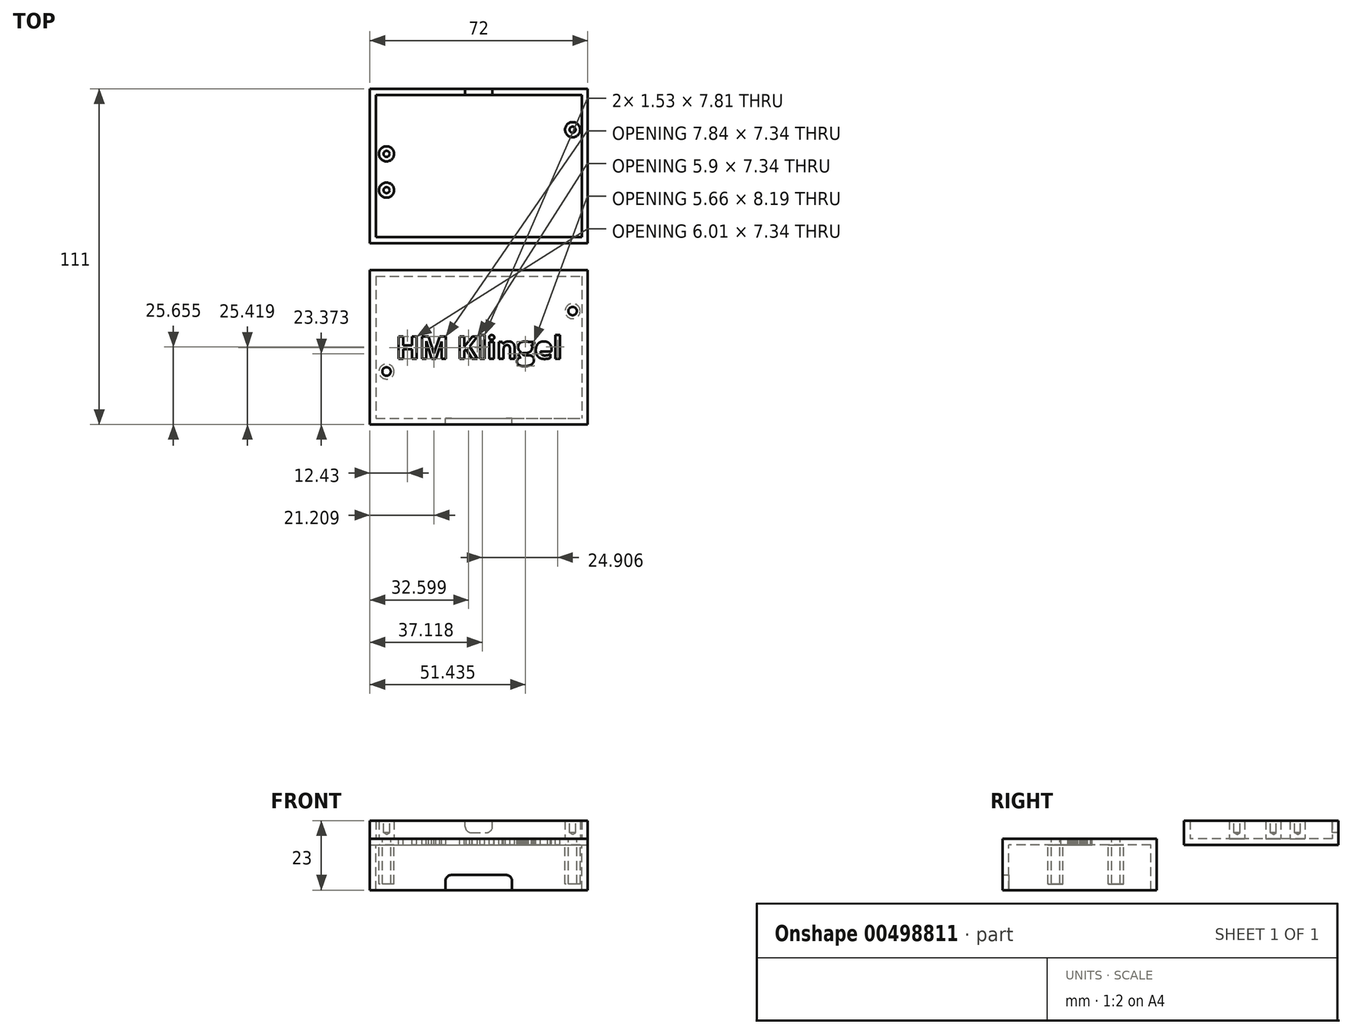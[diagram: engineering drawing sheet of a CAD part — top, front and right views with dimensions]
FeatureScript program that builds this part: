
annotation { "Feature Type Name" : "Feature", "Feature Type Description" : "" }
export const myFeature = defineFeature(function(context is Context, id is Id, definition is map)
    precondition{}
    {
        {
            var Q0;
            Q0=qCreatedBy(makeId("Top.planeOp"),FACE);
            var sketch = newSketch(context, id + "F0", { "sketchPlane" : qUnion([Q0])});
            skLineSegment(sketch, "E0.bottom", {"start": v(-45.23, 18.38) * mm, "end": v(22.77, 18.38) * mm});
            skLineSegment(sketch, "E0.top", {"start": v(-45.23, -28.62) * mm, "end": v(22.77, -28.62) * mm});
            skLineSegment(sketch, "E0.left", {"start": v(-45.23, 18.38) * mm, "end": v(-45.23, -28.62) * mm});
            skLineSegment(sketch, "E0.right", {"start": v(22.77, 18.38) * mm, "end": v(22.77, -28.62) * mm});
            skLineSegment(sketch, "E1.bottom", {"start": v(-47.23, 20.38) * mm, "end": v(24.77, 20.38) * mm});
            skLineSegment(sketch, "E1.top", {"start": v(-47.23, -30.62) * mm, "end": v(24.77, -30.62) * mm});
            skLineSegment(sketch, "E1.left", {"start": v(-47.23, 20.38) * mm, "end": v(-47.23, -30.62) * mm});
            skLineSegment(sketch, "E1.right", {"start": v(24.77, 20.38) * mm, "end": v(24.77, -30.62) * mm});
            skLineSegment(sketch, "E2", {"start": v(-11.23, 20.38) * mm, "end": v(-11.23, 18.38) * mm, "construction": true});
            skLineSegment(sketch, "E3", {"start": v(24.77, -5.12) * mm, "end": v(22.77, -5.12) * mm, "construction": true});
            skLineSegment(sketch, "E4", {"start": v(-45.23, -5.12) * mm, "end": v(-47.23, -5.12) * mm, "construction": true});
            skLineSegment(sketch, "E5", {"start": v(-11.23, -30.62) * mm, "end": v(-11.23, -28.62) * mm, "construction": true});
            skLineSegment(sketch, "E6", {"start": v(19.77, -28.62) * mm, "end": v(19.77, 6.88) * mm, "construction": true});
            skLineSegment(sketch, "E7", {"start": v(19.77, 6.88) * mm, "end": v(22.77, 6.88) * mm, "construction": true});
            skCircle(sketch, "E8", {"center": v(19.77, 6.88) * mm, "radius": 2.5 * mm});
            skLineSegment(sketch, "E9", {"start": v(-41.73, -28.62) * mm, "end": v(-41.73, -1.12) * mm, "construction": true});
            skLineSegment(sketch, "E10", {"start": v(-41.73, -1.12) * mm, "end": v(-45.23, -1.12) * mm, "construction": true});
            skCircle(sketch, "E11", {"center": v(-41.73, -1.12) * mm, "radius": 2.5 * mm});
            skPoint(sketch, "E12", {"position": v(-41.73, -13.12) * mm});
            skCircle(sketch, "E13", {"center": v(-41.73, -13.12) * mm, "radius": 2.5 * mm});
            skSolve(sketch);
        }
        {
            var Q0;
            Q0=makeQuery(id+"F0.imprint","IMPRINT",FACE,{"disambiguationData":[TD([[makeQuery(id+"F0.imprint","IMPRINT",EDGE,{"derivedFrom":sQuery(id+"F0.wireOp",EDGE,"E0.bottom")}),1.0]])]});
            var Q1;
            Q1=makeQuery(id+"F0.imprint","IMPRINT",FACE,{"disambiguationData":[TD([[makeQuery(id+"F0.imprint","IMPRINT",EDGE,{"derivedFrom":sQuery(id+"F0.wireOp",EDGE,"E11")}),1.0]])]});
            var Q2;
            Q2=makeQuery(id+"F0.imprint","IMPRINT",FACE,{"disambiguationData":[TD([[makeQuery(id+"F0.imprint","IMPRINT",EDGE,{"derivedFrom":sQuery(id+"F0.wireOp",EDGE,"E8")}),1.0]])]});
            var Q3;
            Q3=makeQuery(id+"F0.imprint","IMPRINT",FACE,{"disambiguationData":[TD([[makeQuery(id+"F0.imprint","IMPRINT",EDGE,{"derivedFrom":sQuery(id+"F0.wireOp",EDGE,"E0.bottom")}),-1.0]])]});
            var Q4;
            Q4=makeQuery(id+"F0.imprint","IMPRINT",FACE,{"disambiguationData":[TD([[makeQuery(id+"F0.imprint","IMPRINT",EDGE,{"derivedFrom":sQuery(id+"F0.wireOp",EDGE,"E13")}),1.0]])]});
            extrude(context, id + "F1", {"entities" : qUnion([Q0, Q1, Q2, Q3, Q4]), "oppositeDirection" : true, "depth" : 2 * mm});
        }
        {
            var Q0;
            Q0=makeQuery(id+"F1.opExtrude","SWEPT_BODY",BODY,{"disambiguationData":[OSD([sQuery(id+"F0.wireOp",EDGE,"E1.bottom"),sQuery(id+"F0.wireOp",EDGE,"E1.top"),sQuery(id+"F0.wireOp",EDGE,"E1.left"),sQuery(id+"F0.wireOp",EDGE,"E1.right")])]});
            var Q1;
            Q1=qCreatedBy(makeId("Front.planeOp"),FACE);
            transform(context, id + "F2", {"entities" : qUnion([Q0]), "transformType" : TransformType.TRANSLATION_DISTANCE, "transformDirection" : qUnion([Q1]), "distance" : 60 * mm, "makeCopy" : true});
        }
        {
            var Q0;
            Q0=makeQuery(id+"F2.opPattern","COPY",FACE,{"derivedFrom":makeQuery(id+"F1.opExtrude","CAP_FACE",FACE,{"disambiguationData":[OSD([sQuery(id+"F0.wireOp",EDGE,"E1.bottom"),sQuery(id+"F0.wireOp",EDGE,"E1.top"),sQuery(id+"F0.wireOp",EDGE,"E1.left"),sQuery(id+"F0.wireOp",EDGE,"E1.right")])],"isStart":true}),"instanceName":"1"});
            var sketch = newSketch(context, id + "F3", { "sketchPlane" : qUnion([Q0])});
            skLineSegment(sketch, "E14.bottom", {"start": v(-47.23, -39.62) * mm, "end": v(24.77, -39.62) * mm});
            skLineSegment(sketch, "E14.top", {"start": v(-47.23, -90.62) * mm, "end": v(24.77, -90.62) * mm});
            skLineSegment(sketch, "E14.left", {"start": v(-47.23, -39.62) * mm, "end": v(-47.23, -90.62) * mm});
            skLineSegment(sketch, "E14.right", {"start": v(24.77, -39.62) * mm, "end": v(24.77, -90.62) * mm});
            skLineSegment(sketch, "E15.bottom", {"start": v(-45.23, -41.62) * mm, "end": v(22.77, -41.62) * mm});
            skLineSegment(sketch, "E15.top", {"start": v(-45.23, -88.62) * mm, "end": v(22.77, -88.62) * mm});
            skLineSegment(sketch, "E15.left", {"start": v(-45.23, -41.62) * mm, "end": v(-45.23, -88.62) * mm});
            skLineSegment(sketch, "E15.right", {"start": v(22.77, -41.62) * mm, "end": v(22.77, -88.62) * mm});
            skLineSegment(sketch, "E16", {"start": v(-22.26, -39.62) * mm, "end": v(-22.26, -41.62) * mm, "construction": true});
            skLineSegment(sketch, "E17", {"start": v(-45.23, -56.12) * mm, "end": v(-47.23, -56.12) * mm, "construction": true});
            skLineSegment(sketch, "E18", {"start": v(-15.24, -88.62) * mm, "end": v(-15.24, -90.62) * mm, "construction": true});
            skLineSegment(sketch, "E19", {"start": v(22.77, -57.03) * mm, "end": v(24.77, -57.03) * mm, "construction": true});
            skLineSegment(sketch, "E20", {"start": v(-45.23, -61.12) * mm, "end": v(-41.73, -61.12) * mm, "construction": true});
            skLineSegment(sketch, "E21", {"start": v(-41.73, -61.12) * mm, "end": v(-41.73, -88.62) * mm, "construction": true});
            skLineSegment(sketch, "E22", {"start": v(22.77, -53.12) * mm, "end": v(19.77, -53.12) * mm, "construction": true});
            skLineSegment(sketch, "E23", {"start": v(19.77, -53.12) * mm, "end": v(19.77, -88.62) * mm, "construction": true});
            skCircle(sketch, "E24", {"center": v(19.77, -53.12) * mm, "radius": 2.5 * mm});
            skCircle(sketch, "E25", {"center": v(-41.73, -61.12) * mm, "radius": 2.5 * mm});
            skPoint(sketch, "E26", {"position": v(-41.73, -73.12) * mm});
            skCircle(sketch, "E27", {"center": v(-41.73, -73.12) * mm, "radius": 2.5 * mm});
            skSolve(sketch);
        }
        {
            var Q0;
            Q0=makeQuery(id+"F3.imprint","IMPRINT",FACE,{"disambiguationData":[TD([[makeQuery(id+"F3.imprint","IMPRINT",EDGE,{"derivedFrom":sQuery(id+"F3.wireOp",EDGE,"E14.bottom")}),-1.0]])]});
            extrude(context, id + "F4", {"entities" : qUnion([Q0]), "operationType" : NewBodyOperationType.ADD, "oppositeDirection" : true, "depth" : 17 * mm});
        }
        {
            var Q0;
            Q0=sQuery(id+"F3.wireOp",VERTEX,"E24.center");
            var Q1;
            Q1=sQuery(id+"F3.wireOp",VERTEX,"E26");
            var Q2;
            Q2=makeQuery(id+"F2.opPattern","COPY",BODY,{"derivedFrom":makeQuery(id+"F1.opExtrude","SWEPT_BODY",BODY,{"disambiguationData":[OSD([sQuery(id+"F0.wireOp",EDGE,"E1.bottom"),sQuery(id+"F0.wireOp",EDGE,"E1.top"),sQuery(id+"F0.wireOp",EDGE,"E1.left"),sQuery(id+"F0.wireOp",EDGE,"E1.right")])]}),"instanceName":"1"});
            hole(context, id + "F5", {"style" : HoleStyle.SIMPLE, "endStyle" : HoleEndStyle.BLIND, "holeDiameter" : 3 * mm, "holeDepth" : 3 * mm, "isTappedThrough" : true, "tappedDepth" : 12 * mm, "tapClearance" : 3, "locations" : qUnion([Q0, Q1]), "scope" : qUnion([Q2])});
        }
        {
            var Q0;
            Q0=makeQuery(id+"F4.opExtrude","CAP_FACE",FACE,{"disambiguationData":[OSD([sQuery(id+"F3.wireOp",EDGE,"E14.bottom"),sQuery(id+"F3.wireOp",EDGE,"E14.top"),sQuery(id+"F3.wireOp",EDGE,"E14.left"),sQuery(id+"F3.wireOp",EDGE,"E14.right"),sQuery(id+"F3.wireOp",EDGE,"E15.bottom"),sQuery(id+"F3.wireOp",EDGE,"E15.top"),sQuery(id+"F3.wireOp",EDGE,"E15.left"),sQuery(id+"F3.wireOp",EDGE,"E15.right")])],"isStart":false});
            var sketch = newSketch(context, id + "F6", { "sketchPlane" : qUnion([Q0])});
            skLineSegment(sketch, "E28.bottom", {"start": v(-22.23, 90.62) * mm, "end": v(-0.23, 90.62) * mm});
            skLineSegment(sketch, "E28.top", {"start": v(-22.23, 88.62) * mm, "end": v(-0.23, 88.62) * mm});
            skLineSegment(sketch, "E28.left", {"start": v(-22.23, 90.62) * mm, "end": v(-22.23, 88.62) * mm});
            skLineSegment(sketch, "E28.right", {"start": v(-0.23, 90.62) * mm, "end": v(-0.23, 88.62) * mm});
            skLineSegment(sketch, "E29", {"start": v(-47.23, 88.62) * mm, "end": v(-22.23, 88.62) * mm});
            skLineSegment(sketch, "E30", {"start": v(-0.23, 88.62) * mm, "end": v(24.77, 88.62) * mm});
            skSolve(sketch);
        }
        {
            var Q0;
            Q0=makeQuery(id+"F6.imprint","IMPRINT",FACE,{"disambiguationData":[TD([[makeQuery(id+"F6.imprint","IMPRINT",EDGE,{"derivedFrom":sQuery(id+"F6.wireOp",EDGE,"E28.bottom")}),-1.0]])]});
            extrude(context, id + "F7", {"entities" : qUnion([Q0]), "operationType" : NewBodyOperationType.REMOVE, "oppositeDirection" : true, "depth" : 5 * mm});
        }
        {
            var Q0;
            Q0=makeQuery(id+"F7.boolean.opBoolean","COPY",EDGE,{"derivedFrom":makeQuery(id+"F7.opExtrude","CAP_EDGE",EDGE,{"disambiguationData":[OSD([sQuery(id+"F6.wireOp",EDGE,"E28.left")])],"isStart":false})});
            var Q1;
            Q1=makeQuery(id+"F7.boolean.opBoolean","COPY",EDGE,{"derivedFrom":makeQuery(id+"F7.opExtrude","CAP_EDGE",EDGE,{"disambiguationData":[OSD([sQuery(id+"F6.wireOp",EDGE,"E28.right")])],"isStart":false})});
            fillet(context, id + "F8", {"entities" : qUnion([Q0, Q1]), "radius" : 2 * mm, "tangentPropagation" : true, "allowEdgeOverflow" : false});
        }
        {
            var Q0;
            Q0=makeQuery(id+"F2.opPattern","COPY",FACE,{"derivedFrom":makeQuery(id+"F1.opExtrude","CAP_FACE",FACE,{"disambiguationData":[OSD([sQuery(id+"F0.wireOp",EDGE,"E1.bottom"),sQuery(id+"F0.wireOp",EDGE,"E1.top"),sQuery(id+"F0.wireOp",EDGE,"E1.left"),sQuery(id+"F0.wireOp",EDGE,"E1.right")])],"isStart":true}),"instanceName":"1"});
            var sketch = newSketch(context, id + "F9", { "sketchPlane" : qUnion([Q0])});
            skText(sketch, "E31", { "text": "HM Klingel", "fontName": "OpenSans-Bold.ttf"});
            skLineSegment(sketch, "E32", {"start": v(-38.73, -65.16) * mm, "end": v(-47.23, -65.16) * mm, "construction": true});
            skLineSegment(sketch, "E33", {"start": v(16.27, -65.16) * mm, "end": v(24.77, -65.16) * mm, "construction": true});
            skLineSegment(sketch, "E34", {"start": v(-13.7, -39.62) * mm, "end": v(-13.7, -61.46) * mm, "construction": true});
            skLineSegment(sketch, "E35", {"start": v(-18.1, -68.87) * mm, "end": v(-20.06, -90.62) * mm, "construction": true});
            const initialGuessF9  = {"E31": [-0.03873, -0.06887, 1, 0, 0.0074]};
            skSetInitialGuess(sketch, initialGuessF9);
            skSolve(sketch);
        }
        {
            var Q0;
            Q0 = qSketchRegion(id + "F9", true);
            extrude(context, id + "F10", {"entities" : qUnion([Q0]), "operationType" : NewBodyOperationType.REMOVE, "oppositeDirection" : true, "depth" : 2 * mm});
        }
        {
            var Q0;
            Q0=makeQuery(id+"F0.imprint","IMPRINT",FACE,{"disambiguationData":[TD([[makeQuery(id+"F0.imprint","IMPRINT",EDGE,{"derivedFrom":sQuery(id+"F0.wireOp",EDGE,"E0.bottom")}),1.0]])]});
            var Q1;
            Q1=makeQuery(id+"F0.imprint","IMPRINT",FACE,{"disambiguationData":[TD([[makeQuery(id+"F0.imprint","IMPRINT",EDGE,{"derivedFrom":sQuery(id+"F0.wireOp",EDGE,"E11")}),1.0]])]});
            var Q2;
            Q2=makeQuery(id+"F0.imprint","IMPRINT",FACE,{"disambiguationData":[TD([[makeQuery(id+"F0.imprint","IMPRINT",EDGE,{"derivedFrom":sQuery(id+"F0.wireOp",EDGE,"E13")}),1.0]])]});
            var Q3;
            Q3=makeQuery(id+"F0.imprint","IMPRINT",FACE,{"disambiguationData":[TD([[makeQuery(id+"F0.imprint","IMPRINT",EDGE,{"derivedFrom":sQuery(id+"F0.wireOp",EDGE,"E8")}),1.0]])]});
            extrude(context, id + "F11", {"entities" : qUnion([Q0, Q1, Q2, Q3]), "operationType" : NewBodyOperationType.ADD, "depth" : 6 * mm});
        }
        {
            var Q0;
            Q0=makeQuery(id+"F3.imprint","IMPRINT",FACE,{"disambiguationData":[TD([[makeQuery(id+"F3.imprint","IMPRINT",EDGE,{"derivedFrom":sQuery(id+"F3.wireOp",EDGE,"E24")}),1.0]])]});
            var Q1;
            Q1=makeQuery(id+"F3.imprint","IMPRINT",FACE,{"disambiguationData":[TD([[makeQuery(id+"F3.imprint","IMPRINT",EDGE,{"derivedFrom":sQuery(id+"F3.wireOp",EDGE,"E27")}),1.0]])]});
            extrude(context, id + "F12", {"entities" : qUnion([Q0, Q1]), "operationType" : NewBodyOperationType.ADD, "oppositeDirection" : true, "depth" : 15 * mm});
        }
        {
            var Q0;
            Q0=sQuery(id+"F3.wireOp",VERTEX,"E26");
            var Q1;
            Q1=sQuery(id+"F3.wireOp",VERTEX,"E24.center");
            var Q2;
            Q2=makeQuery(id+"F10.boolean.opBoolean","SPLIT",BODY,{"disambiguationData":[OD(0.0)],"derivedFrom":makeQuery(id+"F2.opPattern","COPY",BODY,{"derivedFrom":makeQuery(id+"F1.opExtrude","SWEPT_BODY",BODY,{"disambiguationData":[OSD([sQuery(id+"F0.wireOp",EDGE,"E1.bottom"),sQuery(id+"F0.wireOp",EDGE,"E1.top"),sQuery(id+"F0.wireOp",EDGE,"E1.left"),sQuery(id+"F0.wireOp",EDGE,"E1.right")])]}),"instanceName":"1"})});
            hole(context, id + "F13", {"style" : HoleStyle.SIMPLE, "endStyle" : HoleEndStyle.BLIND, "holeDiameter" : 2.8 * mm, "holeDepth" : 20 * mm, "isTappedThrough" : true, "tappedDepth" : 12 * mm, "tapClearance" : 3, "locations" : qUnion([Q0, Q1]), "scope" : qUnion([Q2])});
        }
        {
            var Q0;
            Q0=makeQuery(id+"F11.opExtrude","CAP_FACE",FACE,{"disambiguationData":[OSD([sQuery(id+"F0.wireOp",EDGE,"E11")])],"isStart":false});
            var sketch = newSketch(context, id + "F14", { "sketchPlane" : qUnion([Q0])});
            skPoint(sketch, "E36", {"position": v(-41.73, -1.12) * mm});
            skSolve(sketch);
        }
        {
            var Q0;
            Q0=makeQuery(id+"F11.opExtrude","CAP_FACE",FACE,{"disambiguationData":[OSD([sQuery(id+"F0.wireOp",EDGE,"E13")])],"isStart":false});
            var sketch = newSketch(context, id + "F15", { "sketchPlane" : qUnion([Q0])});
            skPoint(sketch, "E37", {"position": v(-41.73, -13.12) * mm});
            skSolve(sketch);
        }
        {
            var Q0;
            Q0=makeQuery(id+"F11.opExtrude","CAP_FACE",FACE,{"disambiguationData":[OSD([sQuery(id+"F0.wireOp",EDGE,"E8")])],"isStart":false});
            var sketch = newSketch(context, id + "F16", { "sketchPlane" : qUnion([Q0])});
            skPoint(sketch, "E38", {"position": v(19.77, 6.88) * mm});
            skSolve(sketch);
        }
        {
            var Q0;
            Q0=sQuery(id+"F14.wireOp",VERTEX,"E36");
            var Q1;
            Q1=sQuery(id+"F15.wireOp",VERTEX,"E37");
            var Q2;
            Q2=sQuery(id+"F16.wireOp",VERTEX,"E38");
            var Q3;
            Q3=makeQuery(id+"F1.opExtrude","SWEPT_BODY",BODY,{"disambiguationData":[OSD([sQuery(id+"F0.wireOp",EDGE,"E1.bottom"),sQuery(id+"F0.wireOp",EDGE,"E1.top"),sQuery(id+"F0.wireOp",EDGE,"E1.left"),sQuery(id+"F0.wireOp",EDGE,"E1.right")])]});
            hole(context, id + "F17", {"style" : HoleStyle.SIMPLE, "endStyle" : HoleEndStyle.BLIND, "holeDiameter" : 2 * mm, "holeDepth" : 4 * mm, "isTappedThrough" : true, "tappedDepth" : 12 * mm, "tapClearance" : 3, "locations" : qUnion([Q0, Q1, Q2]), "scope" : qUnion([Q3])});
        }
        {
            var Q0;
            Q0=makeQuery(id+"F11.opExtrude","CAP_FACE",FACE,{"disambiguationData":[OSD([sQuery(id+"F0.wireOp",EDGE,"E0.bottom"),sQuery(id+"F0.wireOp",EDGE,"E0.top"),sQuery(id+"F0.wireOp",EDGE,"E0.left"),sQuery(id+"F0.wireOp",EDGE,"E0.right"),sQuery(id+"F0.wireOp",EDGE,"E1.bottom"),sQuery(id+"F0.wireOp",EDGE,"E1.top"),sQuery(id+"F0.wireOp",EDGE,"E1.left"),sQuery(id+"F0.wireOp",EDGE,"E1.right")])],"isStart":false});
            var sketch = newSketch(context, id + "F18", { "sketchPlane" : qUnion([Q0])});
            skLineSegment(sketch, "E39.bottom", {"start": v(-15.73, 20.38) * mm, "end": v(-6.73, 20.38) * mm});
            skLineSegment(sketch, "E39.top", {"start": v(-15.73, 18.38) * mm, "end": v(-6.73, 18.38) * mm});
            skLineSegment(sketch, "E39.left", {"start": v(-15.73, 20.38) * mm, "end": v(-15.73, 18.38) * mm});
            skLineSegment(sketch, "E39.right", {"start": v(-6.73, 20.38) * mm, "end": v(-6.73, 18.38) * mm});
            skLineSegment(sketch, "E40", {"start": v(-15.73, 19.38) * mm, "end": v(-47.23, 19.38) * mm, "construction": true});
            skLineSegment(sketch, "E41", {"start": v(-6.73, 19.38) * mm, "end": v(24.77, 19.38) * mm, "construction": true});
            skSolve(sketch);
        }
        {
            var Q0;
            Q0=makeQuery(id+"F18.imprint","IMPRINT",FACE,{"disambiguationData":[TD([[makeQuery(id+"F18.imprint","IMPRINT",EDGE,{"derivedFrom":sQuery(id+"F18.wireOp",EDGE,"E39.bottom")}),-1.0]])]});
            extrude(context, id + "F19", {"entities" : qUnion([Q0]), "operationType" : NewBodyOperationType.REMOVE, "oppositeDirection" : true, "depth" : 4 * mm, "offsetDistance" : 25 * mm});
        }
        {
            var Q0;
            Q0=makeQuery(id+"F19.boolean.opBoolean","COPY",EDGE,{"derivedFrom":makeQuery(id+"F19.opExtrude","CAP_EDGE",EDGE,{"disambiguationData":[OSD([sQuery(id+"F18.wireOp",EDGE,"E39.right")])],"isStart":false})});
            var Q1;
            Q1=makeQuery(id+"F19.boolean.opBoolean","COPY",EDGE,{"derivedFrom":makeQuery(id+"F19.opExtrude","CAP_EDGE",EDGE,{"disambiguationData":[OSD([sQuery(id+"F18.wireOp",EDGE,"E39.left")])],"isStart":false})});
            fillet(context, id + "F20", {"entities" : qUnion([Q0, Q1]), "radius" : 2 * mm, "tangentPropagation" : true, "allowEdgeOverflow" : false});
        }
        {
            var Q0;
            Q0=makeQuery(id+"F9.imprint","IMPRINT",FACE,{"disambiguationData":[TD([[makeQuery(id+"F9.imprint","IMPRINT",EDGE,{"derivedFrom":sQuery(id+"F9.wireOp",EDGE,"E31.sketch_text.stroke-103")}),1.0]])]});
            var Q1;
            Q1=makeQuery(id+"F9.imprint","IMPRINT",FACE,{"disambiguationData":[TD([[makeQuery(id+"F9.imprint","IMPRINT",EDGE,{"derivedFrom":sQuery(id+"F9.wireOp",EDGE,"E31.sketch_text.stroke-112")}),1.0]])]});
            var Q2;
            Q2=makeQuery(id+"F9.imprint","IMPRINT",FACE,{"disambiguationData":[TD([[makeQuery(id+"F9.imprint","IMPRINT",EDGE,{"derivedFrom":sQuery(id+"F9.wireOp",EDGE,"E31.sketch_text.stroke-118")}),1.0]])]});
            extrude(context, id + "F21", {"entities" : qUnion([Q0, Q1, Q2]), "operationType" : NewBodyOperationType.REMOVE, "oppositeDirection" : true, "depth" : 2 * mm});
        }
    });
